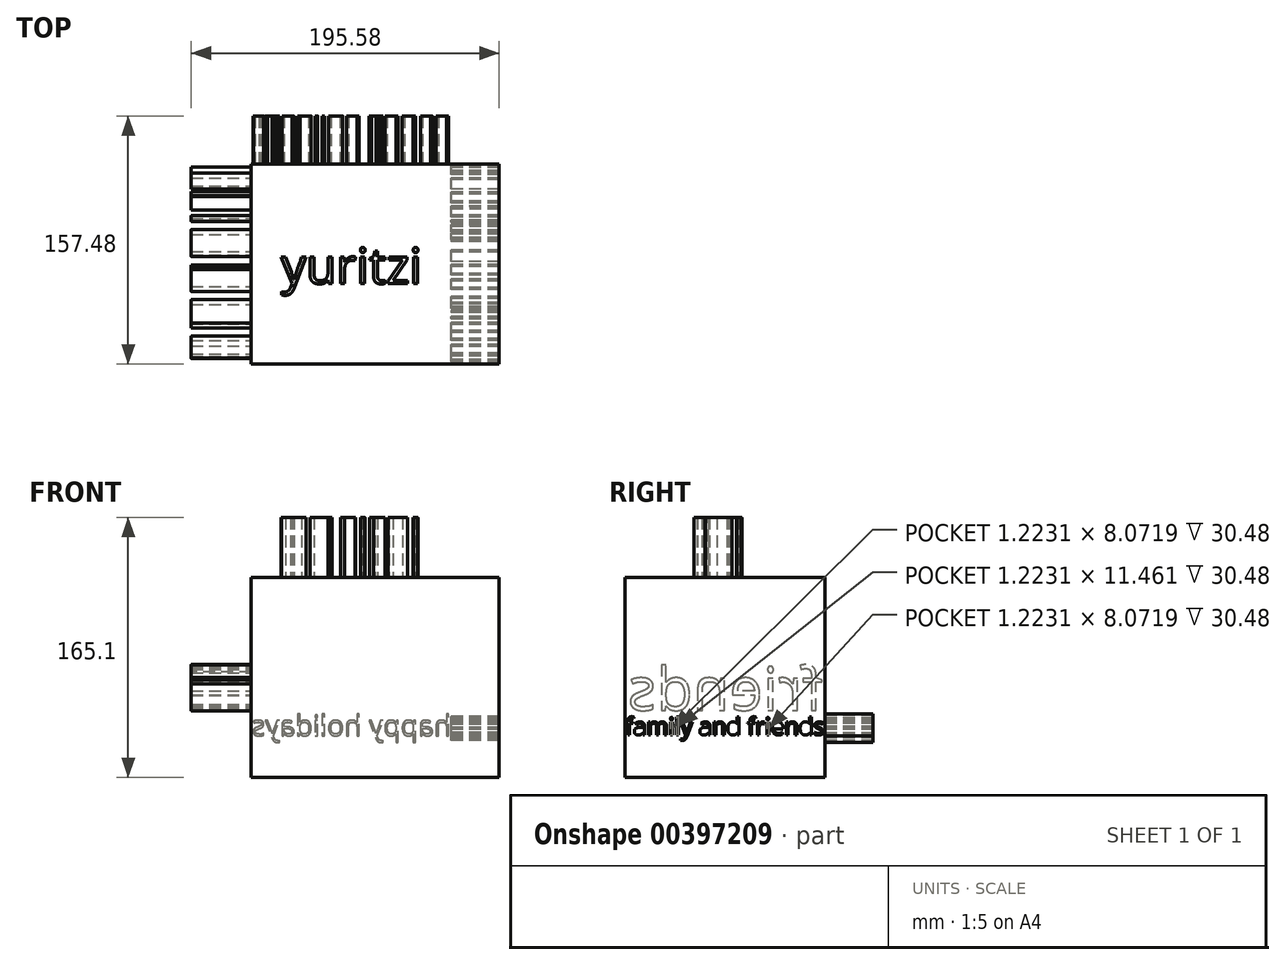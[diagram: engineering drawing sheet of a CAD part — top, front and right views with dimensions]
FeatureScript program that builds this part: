
annotation { "Feature Type Name" : "Feature", "Feature Type Description" : "" }
export const myFeature = defineFeature(function(context is Context, id is Id, definition is map)
    precondition{}
    {
        {
            var Q0;
            Q0=qCreatedBy(makeId("Front.planeOp"),FACE);
            var sketch = newSketch(context, id + "F0", { "sketchPlane" : qUnion([Q0])});
            skLineSegment(sketch, "E0.bottom", {"start": v(-34.12, 8.54) * mm, "end": v(92.88, 8.54) * mm});
            skLineSegment(sketch, "E0.top", {"start": v(-34.12, 135.54) * mm, "end": v(92.88, 135.54) * mm});
            skLineSegment(sketch, "E0.left", {"start": v(-34.12, 8.54) * mm, "end": v(-34.12, 135.54) * mm});
            skLineSegment(sketch, "E0.right", {"start": v(92.88, 8.54) * mm, "end": v(92.88, 135.54) * mm});
            skSolve(sketch);
        }
        {
            var Q0;
            Q0=makeQuery(id+"F0.imprint","IMPRINT",FACE,{"disambiguationData":[TD([[makeQuery(id+"F0.imprint","IMPRINT",EDGE,{"derivedFrom":sQuery(id+"F0.wireOp",EDGE,"E0.bottom")}),1.0]])]});
            extrude(context, id + "F1", {"entities" : qUnion([Q0]), "depth" : 127 * mm});
        }
        {
            var Q0;
            Q0=makeQuery(id+"F1.opExtrude","SWEPT_FACE",FACE,{"disambiguationData":[OSD([sQuery(id+"F0.wireOp",EDGE,"E0.top")])]});
            var sketch = newSketch(context, id + "F2", { "sketchPlane" : qUnion([Q0])});
            skText(sketch, "E1", { "text": "yuritzi", "fontName": "OpenSans-Regular.ttf"});
            const initialGuessF2  = {"E1": [-0.01507, -0.07588, 1, 0, 0.02254]};
            skSetInitialGuess(sketch, initialGuessF2);
            skSolve(sketch);
        }
        {
            var Q0;
            Q0 = qSketchRegion(id + "F2", true);
            extrude(context, id + "F3", {"entities" : qUnion([Q0]), "operationType" : NewBodyOperationType.ADD, "depth" : 38.1 * mm});
        }
        {
            var Q0;
            Q0=makeQuery(id+"F1.opExtrude","SWEPT_FACE",FACE,{"disambiguationData":[OSD([sQuery(id+"F0.wireOp",EDGE,"E0.left")])]});
            var sketch = newSketch(context, id + "F4", { "sketchPlane" : qUnion([Q0])});
            skText(sketch, "E2", { "text": "friends \n", "fontName": "OpenSans-Regular.ttf"});
            const initialGuessF4  = {"E2": [0.0015, 0.05125, 1, 0, 0.02732]};
            skSetInitialGuess(sketch, initialGuessF4);
            skSolve(sketch);
        }
        {
            var Q0;
            Q0 = qSketchRegion(id + "F4", true);
            extrude(context, id + "F5", {"entities" : qUnion([Q0]), "operationType" : NewBodyOperationType.ADD, "depth" : 38.1 * mm});
        }
        {
            var Q0;
            Q0=makeQuery(id+"F1.opExtrude","CAP_FACE",FACE,{"disambiguationData":[OSD([sQuery(id+"F0.wireOp",EDGE,"E0.bottom"),sQuery(id+"F0.wireOp",EDGE,"E0.top"),sQuery(id+"F0.wireOp",EDGE,"E0.left"),sQuery(id+"F0.wireOp",EDGE,"E0.right")])],"isStart":true});
            var sketch = newSketch(context, id + "F6", { "sketchPlane" : qUnion([Q0])});
            skText(sketch, "E3", { "text": "happy holidays", "fontName": "OpenSans-Regular.ttf"});
            const initialGuessF6  = {"E3": [-0.09288, 0.03506, 1, 0, 0.01297]};
            skSetInitialGuess(sketch, initialGuessF6);
            skSolve(sketch);
        }
        {
            var Q0;
            Q0 = qSketchRegion(id + "F6", true);
            extrude(context, id + "F7", {"entities" : qUnion([Q0]), "operationType" : NewBodyOperationType.ADD, "depth" : 30.48 * mm});
        }
        {
            var Q0;
            Q0=makeQuery(id+"F1.opExtrude","SWEPT_FACE",FACE,{"disambiguationData":[OSD([sQuery(id+"F0.wireOp",EDGE,"E0.right")])]});
            var sketch = newSketch(context, id + "F8", { "sketchPlane" : qUnion([Q0])});
            skText(sketch, "E4", { "text": "family and friends", "fontName": "OpenSans-Regular.ttf"});
            const initialGuessF8  = {"E4": [-0.127, 0.03561, 1, 0, 0.01086]};
            skSetInitialGuess(sketch, initialGuessF8);
            skSolve(sketch);
        }
        {
            var Q0;
            Q0=makeQuery(id+"F8.imprint","IMPRINT",FACE,{"disambiguationData":[TD([[makeQuery(id+"F8.imprint","IMPRINT",EDGE,{"derivedFrom":sQuery(id+"F8.wireOp",EDGE,"E4.sketch_text.stroke-0")}),1.0]])]});
            extrude(context, id + "F9", {"entities" : qUnion([Q0]), "operationType" : NewBodyOperationType.ADD, "depth" : 30.48 * mm});
        }
    });
